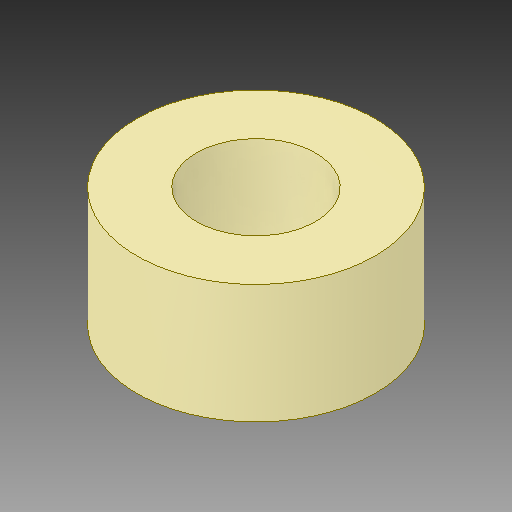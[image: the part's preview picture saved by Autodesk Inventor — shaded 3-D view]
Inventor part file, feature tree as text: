
AUTODESK INVENTOR PART (.ipt)
format: ipt  version: 2019 (Build 230136000, 136)  size: 89,600 bytes
history: native  units: in
note: dims shown in document units (in); Inventor stores cm internally (conversion verified against a paired STEP export)
features: extrude x1, sketch x1
ambient origin geometry x8: Origin, YZ Plane, XZ Plane, XY Plane, X Axis, Y Axis, Z Axis, Center Point
bodies: Solid1 (feature_tree)
feature tree (2):
  extrude  "Extrusion1"  Depth=0.25in
  sketch  "Sketch1"  dims[d0=0.5in d1=0.25in d2=0.25in d3=0.0in]
